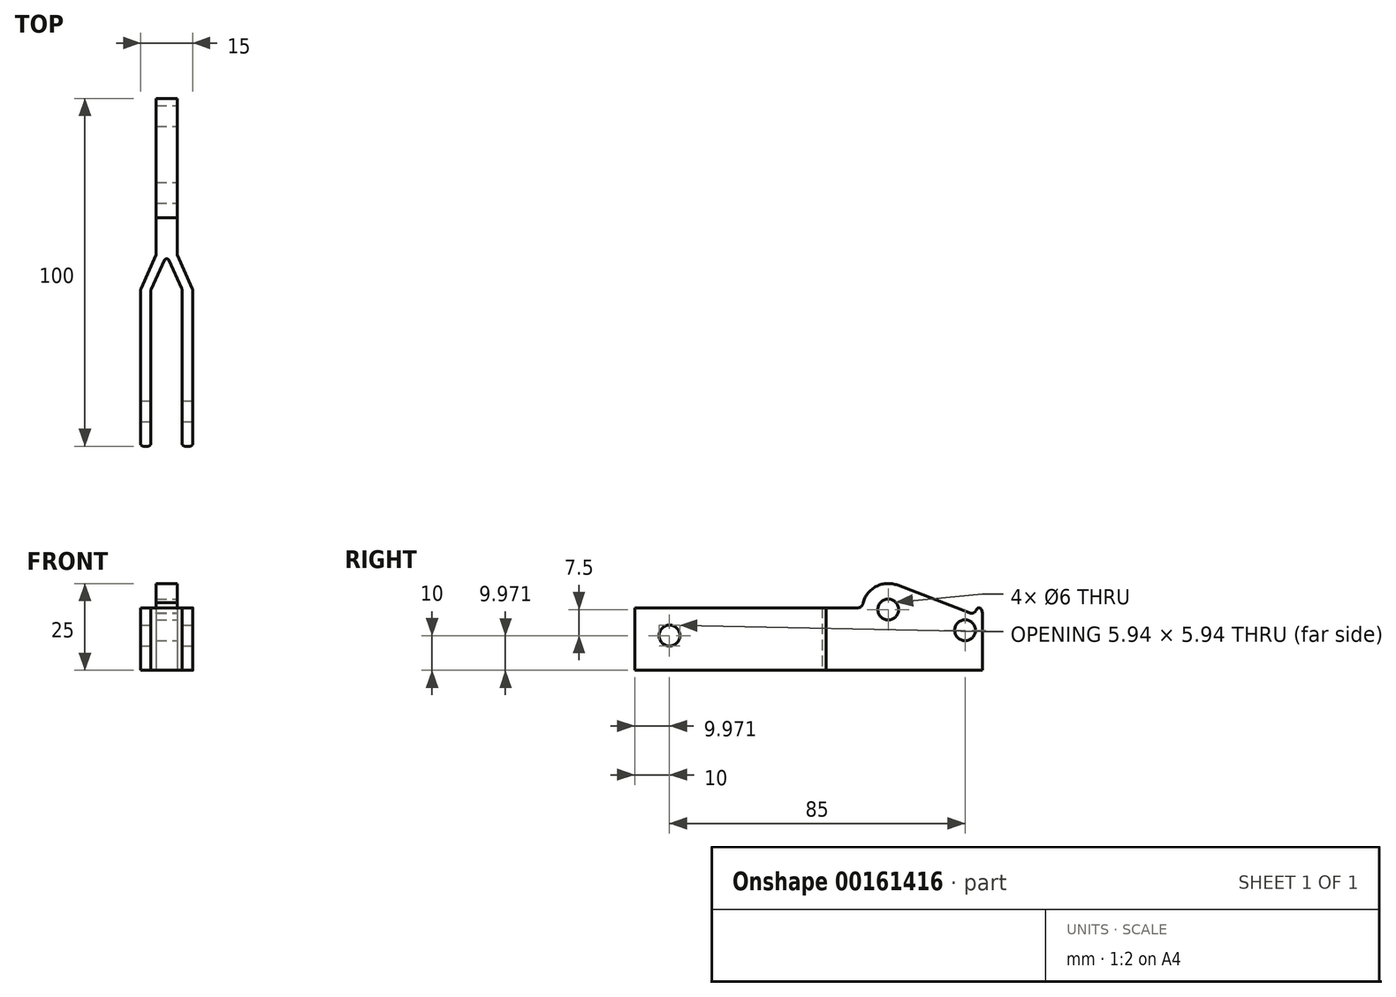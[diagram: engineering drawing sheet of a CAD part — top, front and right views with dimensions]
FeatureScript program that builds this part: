
annotation { "Feature Type Name" : "Feature", "Feature Type Description" : "" }
export const myFeature = defineFeature(function(context is Context, id is Id, definition is map)
    precondition{}
    {
        {
            var Q0;
            Q0=qCreatedBy(makeId("Top.planeOp"),FACE);
            var sketch = newSketch(context, id + "F0", { "sketchPlane" : qUnion([Q0])});
            skLineSegment(sketch, "E0.top", {"start": v(6.75, -22.5) * mm, "end": v(5.18, -22.5) * mm});
            skLineSegment(sketch, "E0.left", {"start": v(7.5, 22.18) * mm, "end": v(7.5, -21.75) * mm});
            skLineSegment(sketch, "E0.right", {"start": v(-7.5, 22.18) * mm, "end": v(-7.5, -21.75) * mm});
            skPoint(sketch, "E0.middle", {"position": v(0, 0) * mm});
            skLineSegment(sketch, "E1.left", {"start": v(-4.57, -21.75) * mm, "end": v(-4.57, 22.03) * mm});
            skLineSegment(sketch, "E1.right", {"start": v(4.43, -21.75) * mm, "end": v(4.43, 22.32) * mm});
            skLineSegment(sketch, "E2.trimOffspring", {"start": v(-5.32, -22.5) * mm, "end": v(-6.75, -22.5) * mm});
            skPoint(sketch, "E3", {"position": v(0, 32.5) * mm});
            skLineSegment(sketch, "E4", {"start": v(-4.43, 22.65) * mm, "end": v(-0.68, 30.98) * mm});
            skLineSegment(sketch, "E5", {"start": v(4.3, 22.94) * mm, "end": v(0.68, 30.98) * mm});
            skLineSegment(sketch, "E6", {"start": v(-7.37, 22.8) * mm, "end": v(-3, 32.5) * mm});
            skLineSegment(sketch, "E7", {"start": v(7.37, 22.8) * mm, "end": v(3, 32.5) * mm});
            skLineSegment(sketch, "E8.top", {"start": v(3, 77.5) * mm, "end": v(-3, 77.5) * mm});
            skLineSegment(sketch, "E8.left", {"start": v(3, 32.5) * mm, "end": v(3, 77.5) * mm});
            skLineSegment(sketch, "E8.right", {"start": v(-3, 32.5) * mm, "end": v(-3, 77.5) * mm});
            skPoint(sketch, "E8.middle", {"position": v(0, 55) * mm});
            skArc(sketch, "E9.filletArc", {"start": v(0.68, 30.98) * mm, "mid": v(0, 31.42) * mm, "end": v(-0.68, 30.98) * mm});
            skPoint(sketch, "E10.visualSharp", {"position": v(-4.57, -22.5) * mm});
            skArc(sketch, "E10.filletArc", {"start": v(-5.32, -22.5) * mm, "mid": v(-4.79, -22.28) * mm, "end": v(-4.57, -21.75) * mm});
            skPoint(sketch, "E11.visualSharp", {"position": v(-7.5, -22.5) * mm});
            skArc(sketch, "E11.filletArc", {"start": v(-7.5, -21.75) * mm, "mid": v(-7.28, -22.28) * mm, "end": v(-6.75, -22.5) * mm});
            skPoint(sketch, "E12.visualSharp", {"position": v(4.43, -22.5) * mm});
            skArc(sketch, "E12.filletArc", {"start": v(4.43, -21.75) * mm, "mid": v(4.65, -22.28) * mm, "end": v(5.18, -22.5) * mm});
            skPoint(sketch, "E13.visualSharp", {"position": v(7.5, -22.5) * mm});
            skArc(sketch, "E13.filletArc", {"start": v(6.75, -22.5) * mm, "mid": v(7.28, -22.28) * mm, "end": v(7.5, -21.75) * mm});
            skPoint(sketch, "E14.visualSharp", {"position": v(-4.57, 22.35) * mm});
            skArc(sketch, "E14.filletArc", {"start": v(-4.43, 22.65) * mm, "mid": v(-4.53, 22.35) * mm, "end": v(-4.57, 22.03) * mm});
            skPoint(sketch, "E15.visualSharp", {"position": v(4.43, 22.65) * mm});
            skArc(sketch, "E15.filletArc", {"start": v(4.43, 22.32) * mm, "mid": v(4.4, 22.64) * mm, "end": v(4.3, 22.94) * mm});
            skPoint(sketch, "E16.visualSharp", {"position": v(7.5, 22.5) * mm});
            skArc(sketch, "E16.filletArc", {"start": v(7.5, 22.18) * mm, "mid": v(7.47, 22.5) * mm, "end": v(7.37, 22.8) * mm});
            skPoint(sketch, "E17.visualSharp", {"position": v(-7.5, 22.5) * mm});
            skArc(sketch, "E17.filletArc", {"start": v(-7.37, 22.8) * mm, "mid": v(-7.47, 22.5) * mm, "end": v(-7.5, 22.18) * mm});
            skSolve(sketch);
        }
        {
            var Q0;
            Q0=qSketchRegion(id+"F0",true);
            extrude(context, id + "F1", {"entities" : qUnion([Q0]), "depth" : 25 * mm});
        }
        {
            var Q0;
            Q0=makeQuery(id+"F1.opExtrude","SWEPT_FACE",FACE,{"disambiguationData":[OSD([sQuery(id+"F0.wireOp",EDGE,"E0.left")])]});
            var sketch = newSketch(context, id + "F2", { "sketchPlane" : qUnion([Q0])});
            skLineSegment(sketch, "E18.bottom", {"start": v(-21.83, 25) * mm, "end": v(43.17, 25) * mm});
            skLineSegment(sketch, "E18.top", {"start": v(-21.83, 18) * mm, "end": v(41.67, 18) * mm});
            skPoint(sketch, "E19.visualSharp", {"position": v(43.17, 18) * mm});
            skArc(sketch, "E19.filletArc", {"start": v(41.67, 18) * mm, "mid": v(42.73, 18.44) * mm, "end": v(43.17, 19.5) * mm});
            skArc(sketch, "E20", {"start": v(53.1, 24.5) * mm, "mid": v(46.73, 24.04) * mm, "end": v(43.02, 18.85) * mm});
            skArc(sketch, "E21", {"start": v(77.21, 17.48) * mm, "mid": v(76.5, 18) * mm, "end": v(75.79, 17.48) * mm});
            skLineSegment(sketch, "E22", {"start": v(77.5, 16.58) * mm, "end": v(77.21, 17.48) * mm});
            skPoint(sketch, "E23.orphan", {"position": v(76.5, 19.73) * mm});
            skLineSegment(sketch, "E24", {"start": v(73.82, 16.53) * mm, "end": v(53.1, 24.5) * mm});
            skPoint(sketch, "E25.visualSharp", {"position": v(75.3, 15.96) * mm});
            skArc(sketch, "E25.filletArc", {"start": v(73.82, 16.53) * mm, "mid": v(75, 16.58) * mm, "end": v(75.79, 17.48) * mm});
            skPoint(sketch, "E26.orphan", {"position": v(77.5, 18) * mm});
            skLineSegment(sketch, "E27", {"start": v(77.5, 16.58) * mm, "end": v(77.5, 25) * mm});
            skLineSegment(sketch, "E28", {"start": v(-21.75, 25) * mm, "end": v(77.5, 25) * mm});
            skCircle(sketch, "E29", {"center": v(50.4, 17.5) * mm, "radius": 3 * mm});
            skLineSegment(sketch, "E30", {"start": v(-21.75, 25) * mm, "end": v(-23.69, 25) * mm});
            skLineSegment(sketch, "E31", {"start": v(-23.69, 25) * mm, "end": v(-23.69, 18) * mm});
            skLineSegment(sketch, "E32", {"start": v(-23.69, 18) * mm, "end": v(-21.83, 18) * mm});
            skCircle(sketch, "E33", {"center": v(-12.5, 10) * mm, "radius": 3 * mm});
            skCircle(sketch, "E34", {"center": v(72.5, 11.53) * mm, "radius": 3 * mm});
            skSolve(sketch);
        }
        {
            var Q0;
            Q0=qSketchRegion(id+"F2",true);
            extrude(context, id + "F3", {"entities" : qUnion([Q0]), "operationType" : NewBodyOperationType.REMOVE, "oppositeDirection" : true, "depth" : 15 * mm});
        }
    });
